# Revit family: Haworth_JanusCafe_Round_Grappa Base
name_source: partatom
category: Furniture
revit_build: Autodesk Revit 2018 (Build: 20170223_1515(x64)
units: mm (PartAtom-declared; Revit-internal decimal feet)

## family parameters
Always vertical = Yes
Cut with Voids When Loaded = No
OmniClass Number = 23.40.70.14.64.21
OmniClass Title = Systems Furniture
Room Calculation Point = No
Shared = No
Work Plane-Based = No

## types (7) — shared parameters
Assembly Code = E2020200
Base Finish = Haworth _ Metal _ JanusCafe _ Brushed Stainless Steel JS1-STLS
Manufacturer = Haworth
Revision Number = 2
Size = Verify Final Dim. w/ Haworth
URL = http://www.haworth.com
URL - Product = https://www.haworth.com
Warranty = https://www.haworth.com

## per-type parameters (varying)
| type | Actual Depth | Actual Height | Actual Width | Base Radius | Description | Extra Large | High | Large | Low | Medium | Model | Small | Table Thickness | Top Radius |
| HCJC-JC-GRS1-N4242NH - 29h 42w | 42" | 29 1/2" | 42" | 19 1/2" | Haworth JanusCafe Round Table 42" - Standard Height - Grappa Base | Yes | No | No | Yes | No | HCJC-JC-GRS1-N4242NH | No | 29 1/8" | 21" |
| HCJC-JC-GRS3-N2424NH - 43h 24w | 24" | 43 3/4" | 24" | 10 1/2" | Haworth JanusCafe Round Table 24" - Bar Height - Grappa Base | No | Yes | No | No | No | HCJC-JC-GRS3-N2424NH | Yes | 43 3/8" | 12" |
| HCJC-JC-GRS1-N2424NH - 29h 24w | 24" | 29 1/2" | 24" | 10 1/2" | Haworth JanusCafe Round Table 24" - Standard Height - Grappa Base | No | No | No | Yes | No | HCJC-JC-GRS1-N2424NH | Yes | 29 1/8" | 12" |
| HCJC-JC-GRS1-N3030NH - 29h 30w | 30" | 29 1/2" | 30" | 13 1/2" | Haworth JanusCafe Round Table 30" - Standard Height - Grappa Base | No | No | No | Yes | Yes | HCJC-JC-GRS1-N3030NH | No | 29 1/8" | 15" |
| HCJC-JC-GRS3-N3030NH - 43h 30w | 30" | 43 3/4" | 30" | 13 1/2" | Haworth JanusCafe Round Table 30" - Bar Height - Grappa Base | No | Yes | No | No | Yes | HCJC-JC-GRS3-N3030NH | No | 43 3/8" | 15" |
| HCJC-JC-GRS1-N3636NH - 29h 36w | 36" | 29 1/2" | 36" | 16 1/2" | Haworth JanusCafe Round Table 36" - Standard Height - Grappa Base | No | No | Yes | Yes | No | HCJC-JC-GRS1-N3636NH | No | 29 1/8" | 18" |
| HCJC-JC-GRS3-N3636NH - 42h 36w | 36" | 43 3/4" | 36" | 16 1/2" | Haworth JanusCafe Round Table 36" - Bar Height - Grappa Base | No | Yes | Yes | No | No | HCJC-JC-GRS3-N3636NH | No | 43 3/8" | 18" |

## geometry (parser evidence)
native form markers: Sweep x3
no freeform markers — native parametric forms only
